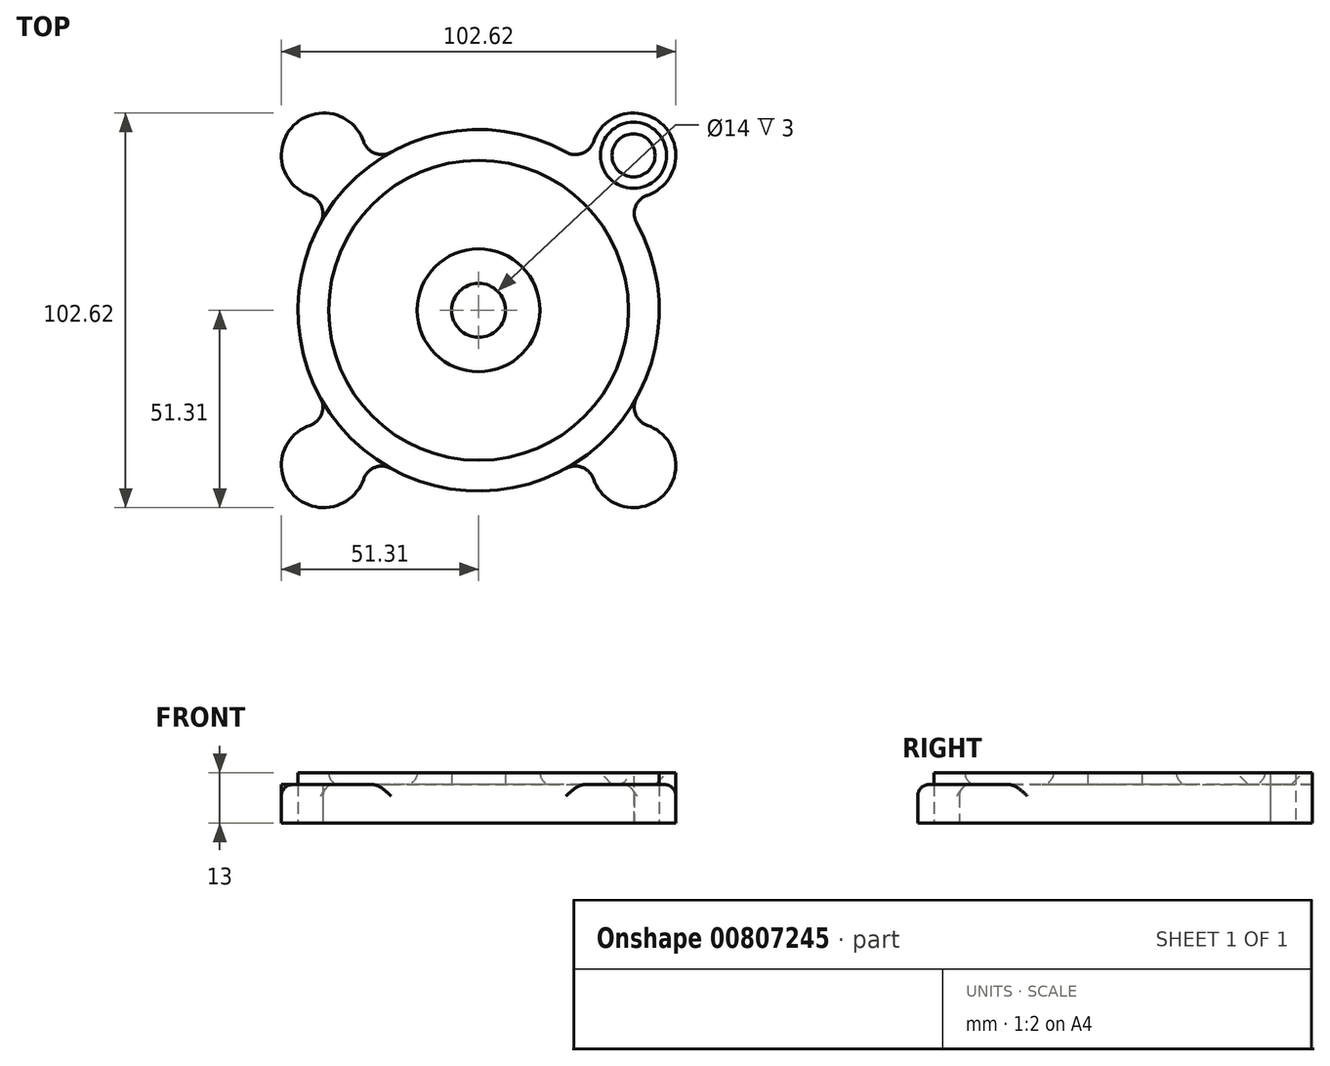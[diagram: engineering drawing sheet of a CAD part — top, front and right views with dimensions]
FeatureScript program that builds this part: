
annotation { "Feature Type Name" : "Feature", "Feature Type Description" : "" }
export const myFeature = defineFeature(function(context is Context, id is Id, definition is map)
    precondition{}
    {
        {
            var Q0;
            Q0=qCreatedBy(makeId("Front.planeOp"),FACE);
            var sketch = newSketch(context, id + "F0", { "sketchPlane" : qUnion([Q0])});
            skLineSegment(sketch, "E0", {"start": v(0, -6.11) * mm, "end": v(0, 21.33) * mm, "construction": true});
            skLineSegment(sketch, "E1", {"start": v(7, 0) * mm, "end": v(16, 0) * mm});
            skLineSegment(sketch, "E2", {"start": v(16, 0) * mm, "end": v(16, 3) * mm});
            skLineSegment(sketch, "E3", {"start": v(16, 3) * mm, "end": v(39, 3) * mm});
            skLineSegment(sketch, "E4", {"start": v(39, 3) * mm, "end": v(39, 0) * mm});
            skLineSegment(sketch, "E5", {"start": v(39, 0) * mm, "end": v(47, 0) * mm});
            skLineSegment(sketch, "E6", {"start": v(47, 0) * mm, "end": v(47, 13) * mm});
            skLineSegment(sketch, "E7", {"start": v(47, 13) * mm, "end": v(39, 13) * mm});
            skLineSegment(sketch, "E8", {"start": v(39, 13) * mm, "end": v(39, 10) * mm});
            skLineSegment(sketch, "E9", {"start": v(39, 10) * mm, "end": v(16, 10) * mm});
            skLineSegment(sketch, "E10", {"start": v(16, 10) * mm, "end": v(16, 13) * mm});
            skLineSegment(sketch, "E11", {"start": v(16, 13) * mm, "end": v(7, 13) * mm});
            skLineSegment(sketch, "E12", {"start": v(7, 13) * mm, "end": v(7, 0) * mm});
            skSolve(sketch);
        }
        {
            var Q0;
            Q0=makeQuery(id+"F0.imprint","IMPRINT",FACE,{"disambiguationData":[TD([[makeQuery(id+"F0.imprint","IMPRINT",EDGE,{"derivedFrom":sQuery(id+"F0.wireOp",EDGE,"E1")}),1.0]])]});
            var Q1;
            Q1=sQuery(id+"F0.wireOp",EDGE,"E0");
            revolve(context, id + "F1", {"surfaceOperationType" : NewSurfaceOperationType.NEW, "entities" : qUnion([Q0]), "axis" : qUnion([Q1]), "revolveType" : RevolveType.FULL});
        }
        {
            var Q0;
            Q0=makeQuery(id+"F1.opRevolve","SWEPT_FACE",FACE,{"disambiguationData":[OSD([sQuery(id+"F0.wireOp",EDGE,"E7")])]});
            var sketch = newSketch(context, id + "F2", { "sketchPlane" : qUnion([Q0])});
            skLineSegment(sketch, "E13", {"start": v(0, 0) * mm, "end": v(59.78, 0) * mm, "construction": true});
            skLineSegment(sketch, "E14", {"start": v(0, 0) * mm, "end": v(53.94, 53.94) * mm, "construction": true});
            skCircle(sketch, "E15", {"center": v(0, 0) * mm, "radius": 57 * mm, "construction": true});
            skCircle(sketch, "E16", {"center": v(40.3, 40.3) * mm, "radius": 11 * mm});
            skSolve(sketch);
        }
        {
            var Q0;
            Q0 = qSketchRegion(id + "F2", true);
            var Q1;
            Q1=makeQuery(id+"F1.opRevolve","SWEPT_FACE",FACE,{"disambiguationData":[OSD([sQuery(id+"F0.wireOp",EDGE,"E5")])]});
            extrude(context, id + "F3", {"entities" : qUnion([Q0]), "operationType" : NewBodyOperationType.ADD, "endBound" : BoundingType.UP_TO_SURFACE, "oppositeDirection" : true, "depth" : 25 * mm, "endBoundEntityFace" : qUnion([Q1]), "offsetDistance" : 25 * mm});
        }
        {
            var Q0;
            Q0=sQuery(id+"F2.wireOp",VERTEX,"E16.center");
            var Q1;
            Q1=makeQuery(id+"F1.opRevolve","SWEPT_BODY",BODY,{"disambiguationData":[OSD([sQuery(id+"F0.wireOp",EDGE,"E1"),sQuery(id+"F0.wireOp",EDGE,"E2"),sQuery(id+"F0.wireOp",EDGE,"E3"),sQuery(id+"F0.wireOp",EDGE,"E4"),sQuery(id+"F0.wireOp",EDGE,"E5"),sQuery(id+"F0.wireOp",EDGE,"E6"),sQuery(id+"F0.wireOp",EDGE,"E7"),sQuery(id+"F0.wireOp",EDGE,"E8"),sQuery(id+"F0.wireOp",EDGE,"E9"),sQuery(id+"F0.wireOp",EDGE,"E10"),sQuery(id+"F0.wireOp",EDGE,"E11"),sQuery(id+"F0.wireOp",EDGE,"E12")])]});
            hole(context, id + "F4", {"style" : HoleStyle.C_SINK, "endStyle" : HoleEndStyle.BLIND, "holeDiameter" : 9 * mm, "cSinkDiameter" : 17.2 * mm, "cSinkAngle" : 90 * degree, "majorDiameter" : 5 * mm, "holeDepth" : 13 * mm, "tappedDepth" : 12 * mm, "tapClearance" : 3, "startFromSketch" : true, "locations" : qUnion([Q0]), "scope" : qUnion([Q1])});
        }
        {
            var Q0;
            Q0=makeQuery(id+"F3.boolean.opBoolean","INTERSECT",EDGE,{"disambiguationData":[OD(0.0)],"derivedFrom":[makeQuery(id+"F1.opRevolve","SWEPT_FACE",FACE,{"disambiguationData":[OSD([sQuery(id+"F0.wireOp",EDGE,"E6")])]}),makeQuery(id+"F3.opExtrude","SWEPT_FACE",FACE,{"disambiguationData":[OSD([sQuery(id+"F2.wireOp",EDGE,"E16")])]})]});
            var Q1;
            Q1=makeQuery(id+"F3.boolean.opBoolean","INTERSECT",EDGE,{"disambiguationData":[OD(1.0)],"derivedFrom":[makeQuery(id+"F1.opRevolve","SWEPT_FACE",FACE,{"disambiguationData":[OSD([sQuery(id+"F0.wireOp",EDGE,"E6")])]}),makeQuery(id+"F3.opExtrude","SWEPT_FACE",FACE,{"disambiguationData":[OSD([sQuery(id+"F2.wireOp",EDGE,"E16")])]})]});
            fillet(context, id + "F5", {"entities" : qUnion([Q0, Q1]), "radius" : 5 * mm, "tangentPropagation" : true, "allowEdgeOverflow" : false});
        }
        {
            var Q0;
            Q0=makeQuery(id+"F1.opRevolve","SWEPT_EDGE",EDGE,{"disambiguationData":[OSD([sQuery(id+"F0.wireOp",EDGE,"E8"),sQuery(id+"F0.wireOp",EDGE,"E9")])]});
            var Q1;
            Q1=makeQuery(id+"F1.opRevolve","SWEPT_EDGE",EDGE,{"disambiguationData":[OSD([sQuery(id+"F0.wireOp",EDGE,"E9"),sQuery(id+"F0.wireOp",EDGE,"E10")])]});
            var Q2;
            Q2=makeQuery(id+"F1.opRevolve","SWEPT_EDGE",EDGE,{"disambiguationData":[OSD([sQuery(id+"F0.wireOp",EDGE,"E3"),sQuery(id+"F0.wireOp",EDGE,"E4")])]});
            var Q3;
            Q3=makeQuery(id+"F1.opRevolve","SWEPT_EDGE",EDGE,{"disambiguationData":[OSD([sQuery(id+"F0.wireOp",EDGE,"E2"),sQuery(id+"F0.wireOp",EDGE,"E3")])]});
            fillet(context, id + "F6", {"entities" : qUnion([Q0, Q1, Q2, Q3]), "radius" : 3 * mm, "tangentPropagation" : true, "allowEdgeOverflow" : false});
        }
        {
            var Q0;
            Q0=qCreatedBy(makeId("Top.planeOp"),FACE);
            var sketch = newSketch(context, id + "F7", { "sketchPlane" : qUnion([Q0])});
            skArc(sketch, "E17.0.0", {"start": v(22.75, 41.13) * mm, "mid": v(0, 47) * mm, "end": v(-22.75, 41.13) * mm});
            skArc(sketch, "E17.0.1", {"start": v(-22.75, 41.13) * mm, "mid": v(-26.97, 40.83) * mm, "end": v(-29.9, 43.88) * mm});
            skArc(sketch, "E17.0.2", {"start": v(-29.9, 43.88) * mm, "mid": v(-48.08, 48.08) * mm, "end": v(-43.88, 29.9) * mm});
            skArc(sketch, "E17.0.3", {"start": v(-43.88, 29.9) * mm, "mid": v(-40.83, 26.97) * mm, "end": v(-41.13, 22.75) * mm});
            skArc(sketch, "E17.0.4", {"start": v(-41.13, 22.75) * mm, "mid": v(-47, 0) * mm, "end": v(-41.13, -22.75) * mm});
            skArc(sketch, "E17.0.5", {"start": v(-41.13, -22.75) * mm, "mid": v(-40.83, -26.97) * mm, "end": v(-43.88, -29.9) * mm});
            skArc(sketch, "E17.0.6", {"start": v(-43.88, -29.9) * mm, "mid": v(-48.08, -48.08) * mm, "end": v(-29.9, -43.88) * mm});
            skArc(sketch, "E17.0.7", {"start": v(-29.9, -43.88) * mm, "mid": v(-26.97, -40.83) * mm, "end": v(-22.75, -41.13) * mm});
            skArc(sketch, "E17.0.8", {"start": v(-22.75, -41.13) * mm, "mid": v(0, -47) * mm, "end": v(22.75, -41.13) * mm});
            skArc(sketch, "E17.0.9", {"start": v(22.75, -41.13) * mm, "mid": v(26.97, -40.83) * mm, "end": v(29.9, -43.88) * mm});
            skArc(sketch, "E17.0.10", {"start": v(29.9, -43.88) * mm, "mid": v(48.08, -48.08) * mm, "end": v(43.88, -29.9) * mm});
            skArc(sketch, "E17.0.11", {"start": v(43.88, -29.9) * mm, "mid": v(40.83, -26.97) * mm, "end": v(41.13, -22.75) * mm});
            skArc(sketch, "E17.0.12", {"start": v(41.13, -22.75) * mm, "mid": v(47, 0) * mm, "end": v(41.13, 22.75) * mm});
            skArc(sketch, "E17.0.13", {"start": v(41.13, 22.75) * mm, "mid": v(40.83, 26.97) * mm, "end": v(43.88, 29.9) * mm});
            skArc(sketch, "E17.0.14", {"start": v(43.88, 29.9) * mm, "mid": v(48.08, 48.08) * mm, "end": v(29.9, 43.88) * mm});
            skArc(sketch, "E17.0.15", {"start": v(29.9, 43.88) * mm, "mid": v(26.97, 40.83) * mm, "end": v(22.75, 41.13) * mm});
            skArc(sketch, "E18", {"start": v(3.42, 46.88) * mm, "mid": v(20.4, 47.24) * mm, "end": v(37, 50.8) * mm});
            skLineSegment(sketch, "E19", {"start": v(0, 0) * mm, "end": v(0, 27.16) * mm, "construction": true});
            skArc(sketch, "E20.MirrorCS", {"start": v(-3.42, 46.88) * mm, "mid": v(-20.4, 47.24) * mm, "end": v(-37, 50.8) * mm});
            skLineSegment(sketch, "E21", {"start": v(0, 0) * mm, "end": v(28.15, 0) * mm, "construction": true});
            skArc(sketch, "E22.MirrorCS", {"start": v(-3.42, -46.88) * mm, "mid": v(-20.4, -47.24) * mm, "end": v(-37, -50.8) * mm});
            skArc(sketch, "E23.MirrorCS", {"start": v(3.42, -46.88) * mm, "mid": v(20.4, -47.24) * mm, "end": v(37, -50.8) * mm});
            skLineSegment(sketch, "E24", {"start": v(-51.3, -40.3) * mm, "end": v(-51.3, 40.3) * mm});
            skLineSegment(sketch, "E25.MirrorCS", {"start": v(51.3, -40.3) * mm, "end": v(51.3, 40.3) * mm});
            skSolve(sketch);
        }
        {
            var Q0;
            {var subQ0=sQuery(id+"F7.wireOp",EDGE,"E17.0.1");Q0=makeQuery(id+"F7.imprint","IMPRINT",FACE,{"disambiguationData":[TD([[makeQuery(id+"F7.imprint","IMPRINT",EDGE,{"derivedFrom":subQ0}),-1.0]])]});}
            var Q1;
            {var subQ0=sQuery(id+"F7.wireOp",EDGE,"E17.0.15");Q1=makeQuery(id+"F7.imprint","IMPRINT",FACE,{"disambiguationData":[TD([[makeQuery(id+"F7.imprint","IMPRINT",EDGE,{"derivedFrom":subQ0}),-1.0]])]});}
            var Q2;
            {var subQ2=sQuery(id+"F7.wireOp",EDGE,"E17.0.11");Q2=makeQuery(id+"F7.imprint","IMPRINT",FACE,{"disambiguationData":[TD([[makeQuery(id+"F7.imprint","IMPRINT",EDGE,{"derivedFrom":subQ2}),-1.0]])]});}
            var Q3;
            {var subQ1=sQuery(id+"F7.wireOp",EDGE,"E17.0.3");Q3=makeQuery(id+"F7.imprint","IMPRINT",FACE,{"disambiguationData":[TD([[makeQuery(id+"F7.imprint","IMPRINT",EDGE,{"derivedFrom":subQ1}),-1.0]])]});}
            var Q4;
            {var subQ0=sQuery(id+"F7.wireOp",EDGE,"E17.0.7");Q4=makeQuery(id+"F7.imprint","IMPRINT",FACE,{"disambiguationData":[TD([[makeQuery(id+"F7.imprint","IMPRINT",EDGE,{"derivedFrom":subQ0}),-1.0]])]});}
            var Q5;
            {var subQ0=sQuery(id+"F7.wireOp",EDGE,"E17.0.9");Q5=makeQuery(id+"F7.imprint","IMPRINT",FACE,{"disambiguationData":[TD([[makeQuery(id+"F7.imprint","IMPRINT",EDGE,{"derivedFrom":subQ0}),-1.0]])]});}
            extrude(context, id + "F8", {"entities" : qUnion([Q0, Q1, Q2, Q3, Q4, Q5]), "operationType" : NewBodyOperationType.ADD, "depth" : 10 * mm, "offsetDistance" : 25 * mm});
        }
        {
            var Q0;
            Q0=makeQuery(id+"F8.opExtrude","CAP_EDGE",EDGE,{"disambiguationData":[OSD([sQuery(id+"F7.wireOp",EDGE,"E17.0.13")])],"isStart":false});
            var Q1;
            Q1=makeQuery(id+"F8.opExtrude","CAP_EDGE",EDGE,{"disambiguationData":[OSD([sQuery(id+"F7.wireOp",EDGE,"E17.0.4")])],"isStart":false});
            var Q2;
            Q2=makeQuery(id+"F8.opExtrude","CAP_EDGE",EDGE,{"disambiguationData":[OSD([sQuery(id+"F7.wireOp",EDGE,"E17.0.7")])],"isStart":false});
            var Q3;
            Q3=makeQuery(id+"F8.opExtrude","CAP_EDGE",EDGE,{"disambiguationData":[OSD([sQuery(id+"F7.wireOp",EDGE,"E17.0.9")])],"isStart":false});
            var Q4;
            {var subQ0=sQuery(id+"F7.wireOp",EDGE,"E17.0.0");Q4=makeQuery(id+"F8.opExtrude","CAP_EDGE",EDGE,{"disambiguationData":[OSD([subQ0]),TDD([makeQuery(id+"F7.imprint","IMPRINT",EDGE,{"disambiguationData":[TD([[makeQuery(id+"F7.imprint","INTERSECT",VERTEX,{"derivedFrom":[subQ0,sQuery(id+"F7.wireOp",EDGE,"E17.0.1")]}),1.0]])],"derivedFrom":subQ0})])],"isStart":false});}
            var Q5;
            {var subQ0=sQuery(id+"F7.wireOp",EDGE,"E17.0.0");Q5=makeQuery(id+"F8.opExtrude","CAP_EDGE",EDGE,{"disambiguationData":[OSD([subQ0]),TDD([makeQuery(id+"F7.imprint","IMPRINT",EDGE,{"disambiguationData":[TD([[makeQuery(id+"F7.imprint","INTERSECT",VERTEX,{"derivedFrom":[subQ0,sQuery(id+"F7.wireOp",EDGE,"E17.0.15")]}),-1.0]])],"derivedFrom":subQ0})])],"isStart":false});}
            fillet(context, id + "F9", {"entities" : qUnion([Q0, Q1, Q2, Q3, Q4, Q5]), "radius" : 3 * mm, "tangentPropagation" : true, "allowEdgeOverflow" : false});
        }
    });
